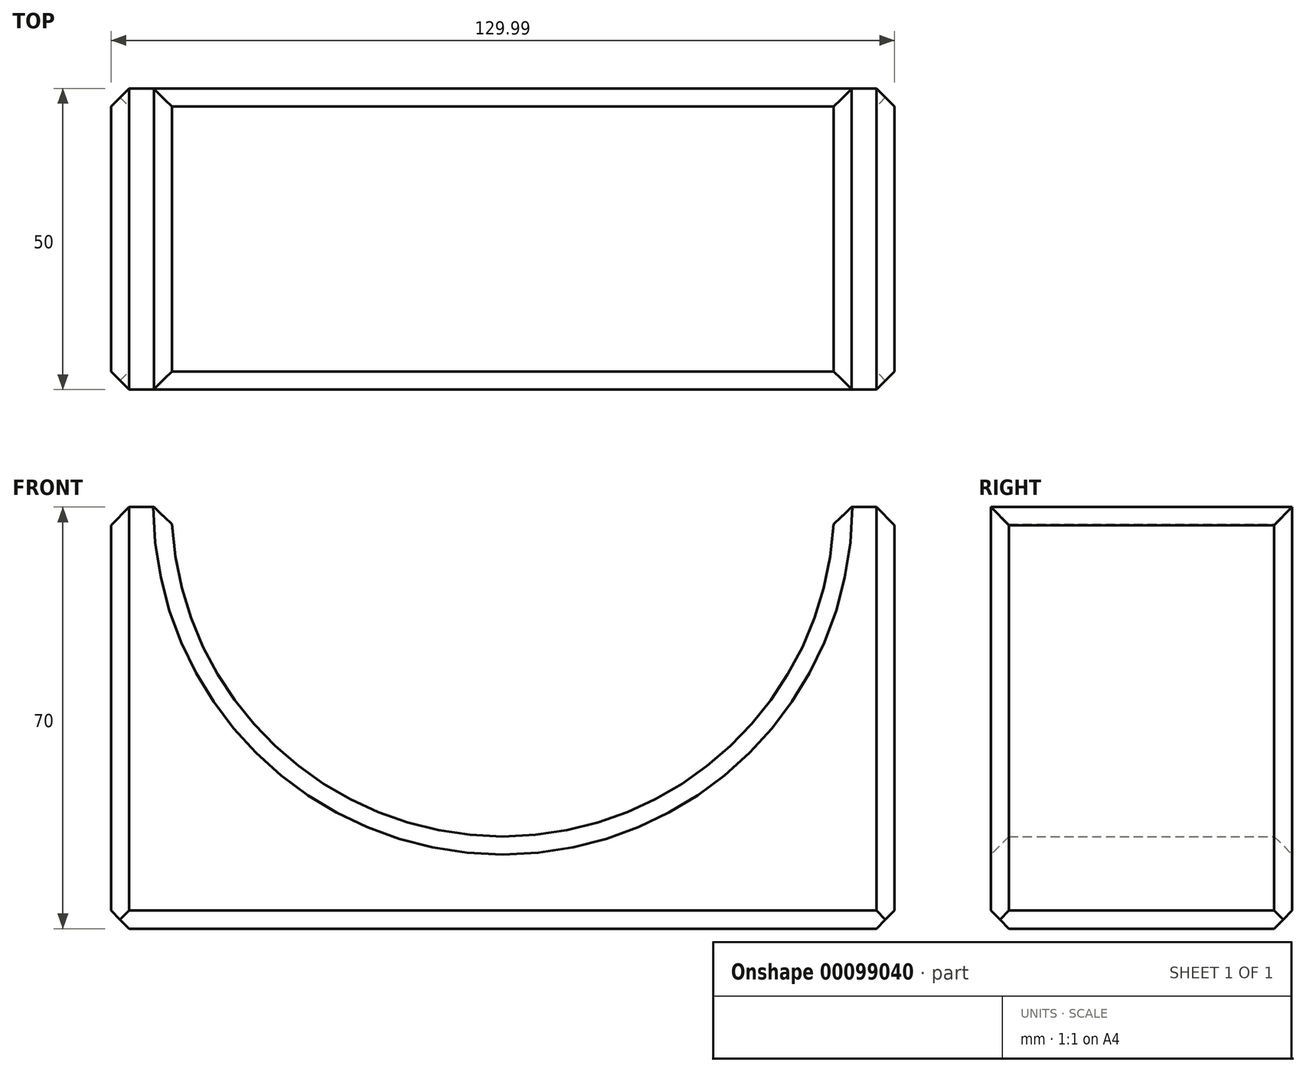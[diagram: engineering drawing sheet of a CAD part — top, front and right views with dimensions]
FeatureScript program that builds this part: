
annotation { "Feature Type Name" : "Feature", "Feature Type Description" : "" }
export const myFeature = defineFeature(function(context is Context, id is Id, definition is map)
    precondition{}
    {
        {
            var Q0;
            Q0=qCreatedBy(makeId("Front.planeOp"),FACE);
            var sketch = newSketch(context, id + "F0", { "sketchPlane" : qUnion([Q0])});
            skLineSegment(sketch, "E0.bottom", {"start": v(-62.88, 33.88) * mm, "end": v(67.11, 33.88) * mm});
            skLineSegment(sketch, "E0.top", {"start": v(-62.88, -36.12) * mm, "end": v(67.11, -36.12) * mm});
            skLineSegment(sketch, "E0.left", {"start": v(-62.88, 33.88) * mm, "end": v(-62.88, -36.12) * mm});
            skLineSegment(sketch, "E0.right", {"start": v(67.11, 33.88) * mm, "end": v(67.11, -36.12) * mm});
            skArc(sketch, "E1", {"start": v(-52.88, 33.88) * mm, "mid": v(2.11, -20.81) * mm, "end": v(57.11, 33.88) * mm});
            skSolve(sketch);
        }
        {
            var Q0;
            Q0=makeQuery(id+"F0.imprint","IMPRINT",FACE,{"disambiguationData":[TD([[makeQuery(id+"F0.imprint","IMPRINT",EDGE,{"derivedFrom":sQuery(id+"F0.wireOp",EDGE,"E0.top")}),1.0]])]});
            extrude(context, id + "F1", {"entities" : qUnion([Q0]), "depth" : 50 * mm});
        }
        {
            var Q0;
            Q0=makeQuery(id+"F1.opExtrude","SWEPT_FACE",FACE,{"disambiguationData":[OSD([sQuery(id+"F0.wireOp",EDGE,"E1")])]});
            chamfer(context, id + "F2", {"entities" : qUnion([Q0]), "width" : 3 * mm, "tangentPropagation" : true});
        }
        {
            var Q0;
            Q0=makeQuery(id+"F1.opExtrude","SWEPT_FACE",FACE,{"disambiguationData":[OSD([sQuery(id+"F0.wireOp",EDGE,"E0.right")])]});
            chamfer(context, id + "F3", {"entities" : qUnion([Q0]), "width" : 3 * mm, "tangentPropagation" : true});
        }
        {
            var Q0;
            Q0=makeQuery(id+"F1.opExtrude","SWEPT_FACE",FACE,{"disambiguationData":[OSD([sQuery(id+"F0.wireOp",EDGE,"E0.left")])]});
            chamfer(context, id + "F4", {"entities" : qUnion([Q0]), "width" : 3 * mm, "tangentPropagation" : true});
        }
        {
            var Q0;
            Q0=makeQuery(id+"F1.opExtrude","CAP_EDGE",EDGE,{"disambiguationData":[OSD([sQuery(id+"F0.wireOp",EDGE,"E0.top")])],"isStart":false});
            var Q1;
            Q1=makeQuery(id+"F1.opExtrude","CAP_EDGE",EDGE,{"disambiguationData":[OSD([sQuery(id+"F0.wireOp",EDGE,"E0.top")])],"isStart":true});
            chamfer(context, id + "F5", {"entities" : qUnion([Q0, Q1]), "width" : 3 * mm, "tangentPropagation" : true});
        }
    });
